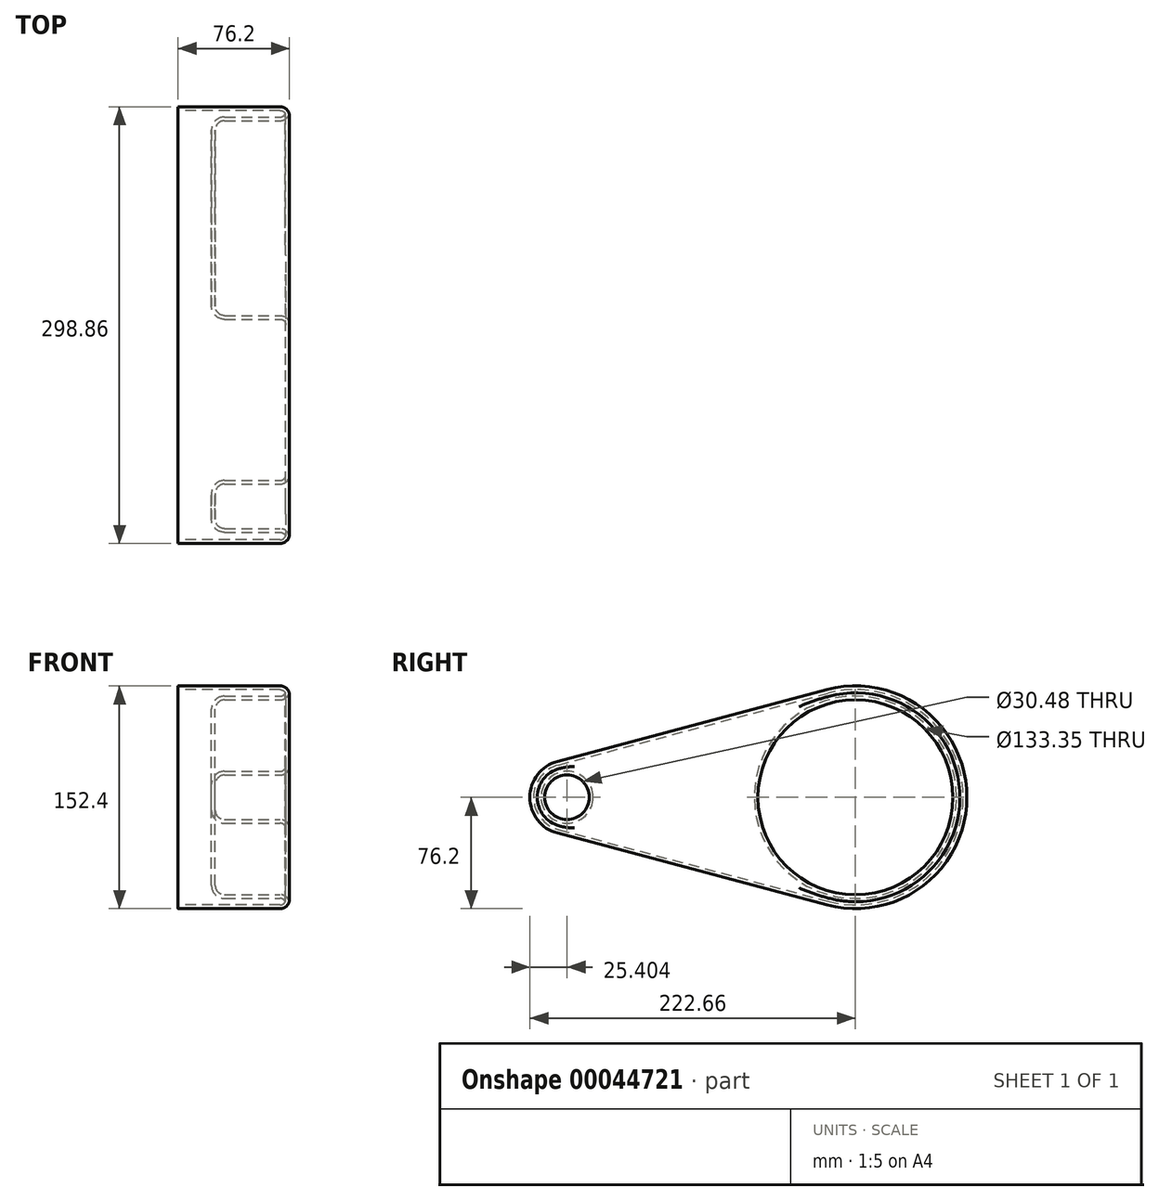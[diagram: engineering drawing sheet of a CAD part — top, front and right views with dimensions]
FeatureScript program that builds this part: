
annotation { "Feature Type Name" : "Feature", "Feature Type Description" : "" }
export const myFeature = defineFeature(function(context is Context, id is Id, definition is map)
    precondition{}
    {
        {
            var Q0;
            Q0=qCreatedBy(makeId("Right.planeOp"),FACE);
            var sketch = newSketch(context, id + "F0", { "sketchPlane" : qUnion([Q0])});
            skCircle(sketch, "E0", {"center": v(0, 0) * mm, "radius": 76.2 * mm});
            skCircle(sketch, "E1", {"center": v(-197.26, 0) * mm, "radius": 25.4 * mm});
            skLineSegment(sketch, "E2", {"start": v(-203.8, 24.54) * mm, "end": v(-7.45, 76.87) * mm});
            skLineSegment(sketch, "E3", {"start": v(-203.8, -24.54) * mm, "end": v(-7.45, -76.87) * mm});
            skSolve(sketch);
        }
        {
            var Q0;
            Q0 = qSketchRegion(id + "F0", true);
            extrude(context, id + "F1", {"entities" : qUnion([Q0]), "depth" : 76.2 * mm});
        }
        {
            var Q0;
            Q0=makeQuery(id+"F1.opExtrude","CAP_FACE",FACE,{"disambiguationData":[OSD([sQuery(id+"F0.wireOp",EDGE,"E0"),sQuery(id+"F0.wireOp",EDGE,"E1"),sQuery(id+"F0.wireOp",EDGE,"E2"),sQuery(id+"F0.wireOp",EDGE,"E3")])],"isStart":false});
            var sketch = newSketch(context, id + "F2", { "sketchPlane" : qUnion([Q0])});
            skCircle(sketch, "E4", {"center": v(0, 0) * mm, "radius": 66.68 * mm});
            skCircle(sketch, "E5", {"center": v(-197.26, 0) * mm, "radius": 15.24 * mm});
            skSolve(sketch);
        }
        {
            var Q0;
            Q0 = qSketchRegion(id + "F2", true);
            extrude(context, id + "F3", {"entities" : qUnion([Q0]), "operationType" : NewBodyOperationType.REMOVE, "oppositeDirection" : true, "depth" : 50.8 * mm});
        }
        {
            var Q0;
            Q0=makeQuery(id+"F1.opExtrude","CAP_FACE",FACE,{"disambiguationData":[OSD([sQuery(id+"F0.wireOp",EDGE,"E0"),sQuery(id+"F0.wireOp",EDGE,"E1"),sQuery(id+"F0.wireOp",EDGE,"E2"),sQuery(id+"F0.wireOp",EDGE,"E3")])],"isStart":false});
            var Q1;
            Q1=makeQuery(id+"F3.boolean.opBoolean","COPY",EDGE,{"derivedFrom":makeQuery(id+"F3.opExtrude","CAP_EDGE",EDGE,{"disambiguationData":[OSD([sQuery(id+"F2.wireOp",EDGE,"E4")])],"isStart":false})});
            var Q2;
            Q2=makeQuery(id+"F3.boolean.opBoolean","COPY",EDGE,{"derivedFrom":makeQuery(id+"F3.opExtrude","CAP_EDGE",EDGE,{"disambiguationData":[OSD([sQuery(id+"F2.wireOp",EDGE,"E5")])],"isStart":false})});
            fillet(context, id + "F4", {"entities" : qUnion([Q0, Q1, Q2]), "radius" : 6.35 * mm, "tangentPropagation" : true, "allowEdgeOverflow" : false});
        }
        {
            var Q0;
            Q0=makeQuery(id+"F1.opExtrude","CAP_FACE",FACE,{"disambiguationData":[OSD([sQuery(id+"F0.wireOp",EDGE,"E0"),sQuery(id+"F0.wireOp",EDGE,"E1"),sQuery(id+"F0.wireOp",EDGE,"E2"),sQuery(id+"F0.wireOp",EDGE,"E3")])],"isStart":true});
            shell(context, id + "F5", {"entities" : qUnion([Q0]), "thickness" : 2.54 * mm});
        }
    });
